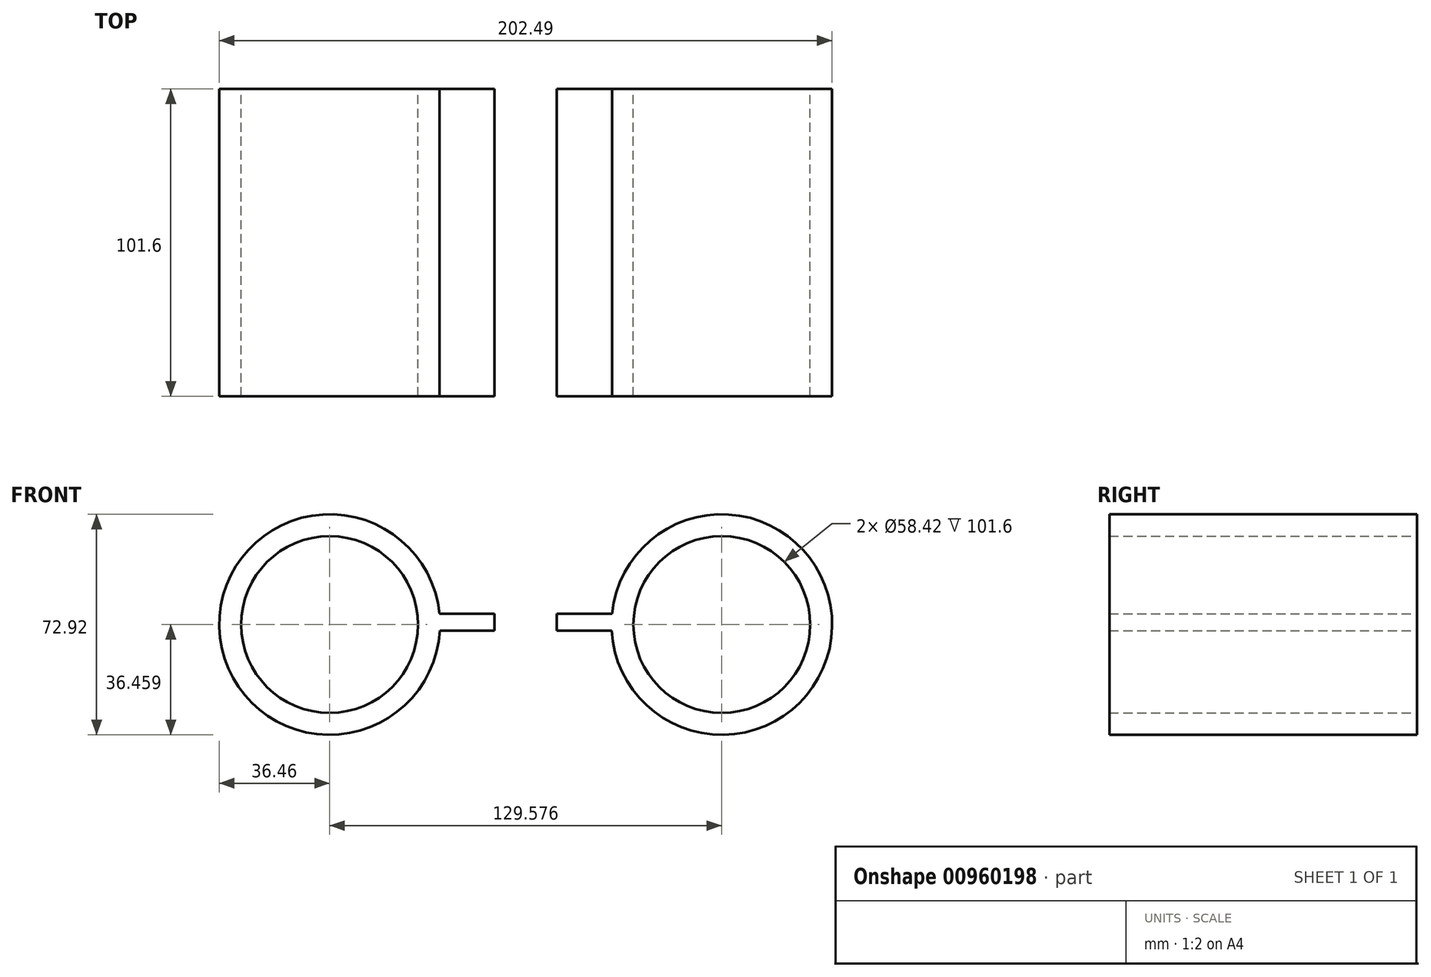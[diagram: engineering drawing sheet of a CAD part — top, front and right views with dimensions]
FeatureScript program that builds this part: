
annotation { "Feature Type Name" : "Feature", "Feature Type Description" : "" }
export const myFeature = defineFeature(function(context is Context, id is Id, definition is map)
    precondition{}
    {
        {
            var Q0;
            Q0=qCreatedBy(makeId("Front.planeOp"),FACE);
            var sketch = newSketch(context, id + "F0", { "sketchPlane" : qUnion([Q0])});
            skPoint(sketch, "E0.middle", {"position": v(0, 0) * mm});
            skCircle(sketch, "E1", {"center": v(3.45, 0.09) * mm, "radius": 36.46 * mm});
            skLineSegment(sketch, "E2.bottom", {"start": v(-32.83, 3.68) * mm, "end": v(-51.03, 3.68) * mm});
            skLineSegment(sketch, "E2.top", {"start": v(-32.83, -1.88) * mm, "end": v(-51.03, -1.88) * mm});
            skLineSegment(sketch, "E2.left", {"start": v(-32.83, 3.68) * mm, "end": v(-32.83, -1.88) * mm});
            skLineSegment(sketch, "E2.right", {"start": v(-51.03, 3.68) * mm, "end": v(-51.03, -1.88) * mm});
            skLineSegment(sketch, "E3.MirrorCS", {"start": v(-89.85, 3.68) * mm, "end": v(-71.65, 3.68) * mm});
            skLineSegment(sketch, "E4.MirrorCS", {"start": v(-71.65, 3.68) * mm, "end": v(-71.65, -1.88) * mm});
            skLineSegment(sketch, "E5.MirrorCS", {"start": v(-89.85, -1.88) * mm, "end": v(-71.65, -1.88) * mm});
            skCircle(sketch, "E6.MirrorC", {"center": v(-126.13, 0.09) * mm, "radius": 36.46 * mm});
            skSolve(sketch);
        }
        {
            var Q0;
            Q0 = qSketchRegion(id + "F0", true);
            extrude(context, id + "F1", {"entities" : qUnion([Q0]), "depth" : 101.6 * mm, "offsetDistance" : 25.4 * mm});
        }
        {
            var Q0;
            Q0=sQuery(id+"F0.wireOp",VERTEX,"E1.center");
            var Q1;
            Q1=makeQuery(id+"F1.opExtrude","SWEPT_BODY",BODY,{"disambiguationData":[OSD([sQuery(id+"F0.wireOp",EDGE,"E1")])]});
            hole(context, id + "F2", {"style" : HoleStyle.SIMPLE, "endStyle" : HoleEndStyle.THROUGH, "oppositeDirection" : true, "holeDiameter" : 58.42 * mm, "majorDiameter" : 6.35 * mm, "isTappedThrough" : true, "tappedDepth" : 12.7 * mm, "tapClearance" : 3, "locations" : qUnion([Q0]), "scope" : qUnion([Q1])});
        }
        {
            var Q0;
            Q0=sQuery(id+"F0.wireOp",VERTEX,"E6.MirrorC.center");
            var Q1;
            Q1=makeQuery(id+"F1.opExtrude","SWEPT_BODY",BODY,{"disambiguationData":[OSD([sQuery(id+"F0.wireOp",EDGE,"E3.MirrorCS"),sQuery(id+"F0.wireOp",EDGE,"E4.MirrorCS"),sQuery(id+"F0.wireOp",EDGE,"E5.MirrorCS"),sQuery(id+"F0.wireOp",EDGE,"E6.MirrorC")])]});
            hole(context, id + "F3", {"style" : HoleStyle.SIMPLE, "endStyle" : HoleEndStyle.THROUGH, "oppositeDirection" : true, "holeDiameter" : 58.42 * mm, "majorDiameter" : 6.35 * mm, "isTappedThrough" : true, "tappedDepth" : 12.7 * mm, "tapClearance" : 3, "locations" : qUnion([Q0]), "scope" : qUnion([Q1])});
        }
    });
